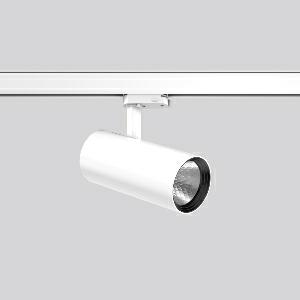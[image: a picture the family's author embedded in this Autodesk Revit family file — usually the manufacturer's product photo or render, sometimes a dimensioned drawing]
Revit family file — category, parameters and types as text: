
# Revit family: deecos_s_mini_742195_002_3_e588
name_source: partatom
category: Lighting Fixtures
units: mm (PartAtom-declared; Revit-internal decimal feet)

## family parameters
Cut with Voids When Loaded = No
Host = Face
Light Source = No
Part Type = Normal
Room Calculation Point = No
Round Connector Dimension = Use Diameter
Shared = No

## types (1)
- DEECOS S mini (1 x LED Modul 935, 2600 lm, 3500)
    Apparent Load = 20 VA
    Approval mark = CE
    CIE Flux Codes = 100 100 100 100 100
    Color Rendering = 92
    Color Temperature = 3500
    Default Elevation = 1800 mm
    Description = Series: DEECOS S mini
LED surface-mounted projector in modern design with no visible cooling ribs. Housing: die-cast aluminium, powder-coated. Rotation range: 356°. Swivel range: 90°. Black plastic ring and recessed LED to prevent glare from the side. Optical assembly with reflector made of MIRO-Silver with 98% total light reflection for outstanding efficiency - can be changed without tools. Best colour rendering index Ra>90. With multi adaptor for 3-circuit tracks 230 V. Suitable for Track on ceiling, Wall track. High quality converter without flickering and stroboscopic effect. The following accessories can be mounted without use of tools: interchangeable lenses, decorative glasses, honeycomb louvre, clear and frosted diffusers, white interchangeable plastic ring. 
Colour: traffic white, matt (RAL 9016)
Diameter: 87 mm
Height: 214 mm
Lamp: LED
Socket: without socket
Colour temperature: 3500K
Colour rendering index (CRI): 92
System power: 20 W
Rated luminous flux: 2600 lm
Luminous efficiency: 130 lm/W
Control gear: Regulated power supply
Protection class: I
Type of protection: IP 20
    Height = 214 mm
    Lamp = 1 x LED Modul 935
    Lamp Light Flux = 2600 lm
    Lamp count = 1
    Length = 87 mm
    Lifetime = 50000 h
    Luminous efficacy = 130 lm/W
    Manufacturer = RZB
    ModVariant = No
    Model = 742195.002.3
    Mounting Place = Ceiling
    Mounting Type = Rail mounted
    Number of Poles = 1
    OnlyDefault = Yes
    Power Factor = 1
    Product Name = DEECOS S mini
    Product group = Track mounted projectors
    ProductGroupID = 301
    Protection Class = Protection class I
    Protection Degree = IP 20
    RLX_Detail_Level = 1
    RLX_Emergency_Light_Flux = 0 lm
    RLX_Emergency_Type = 0
    RLX_Emergency_Type_DB = No
    RlxData = <blob elided: 35341 chars, md5=880a668d>
    Socket = socket
    Standby Power = 0 W
    System Light Flux = 2600 lm
    System Power = 20 W
    Type Comments = Product without accessories
    Type Image = 741926.002.jpg
    URL = http://relux.com
    VarID = ---
    Voltage = 230 V
    Voltage Range = 220-240 V
    Weight = 0.00 kg
    Width = 0 mm  [stored 0 ft]

note: [stored X ft] marks values corroborated as IEEE doubles in the binary element streams (Revit-internal decimal feet)

## geometry (parser evidence)
native form markers: Blend x4, Sweep x10
no freeform markers — native parametric forms only
